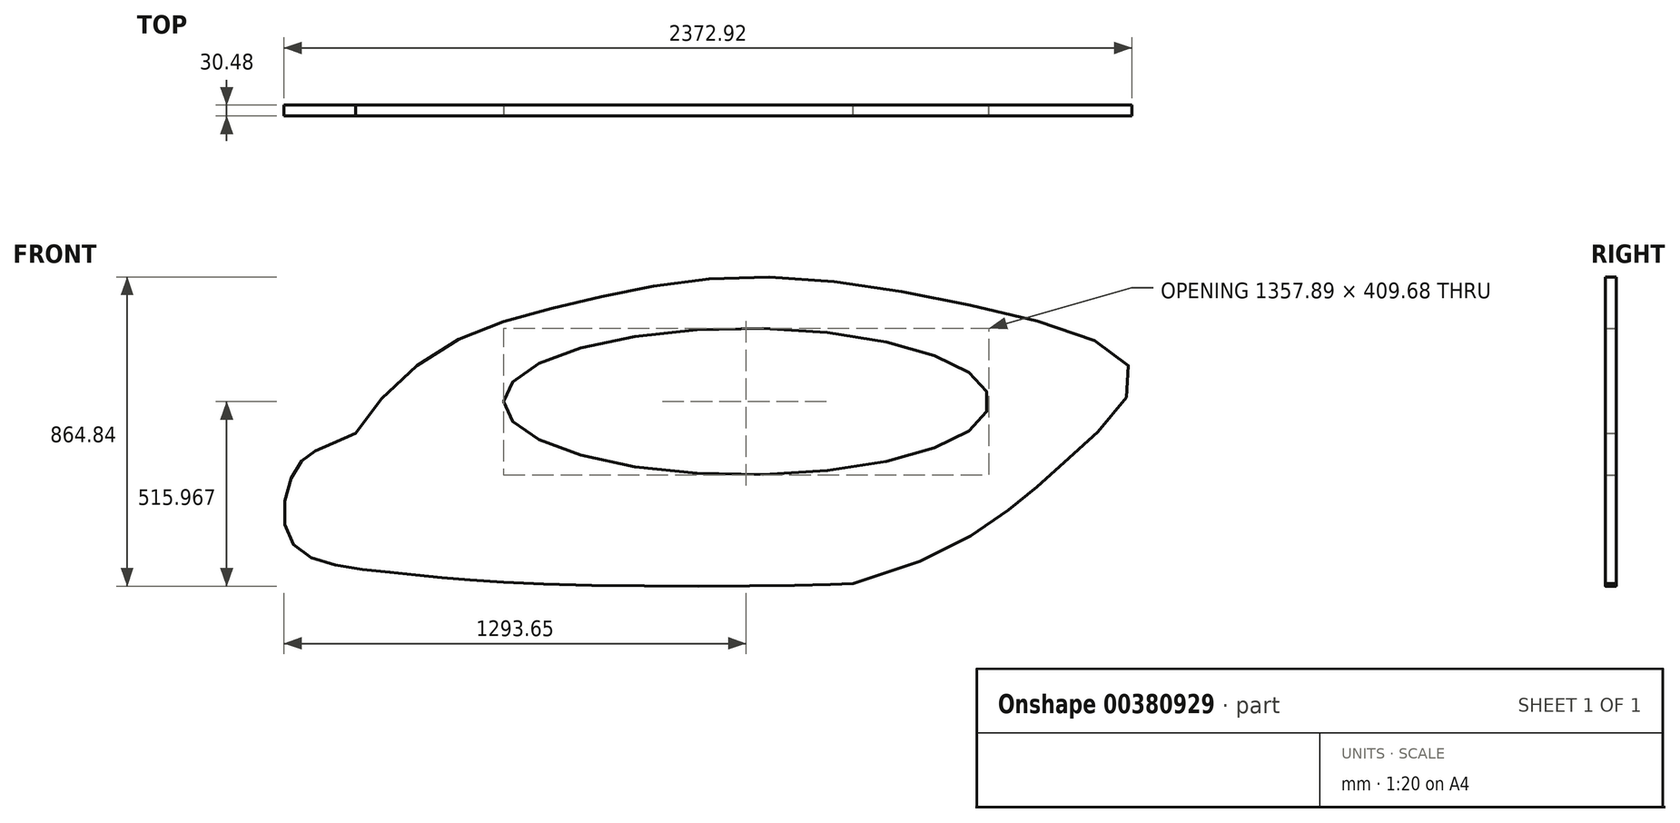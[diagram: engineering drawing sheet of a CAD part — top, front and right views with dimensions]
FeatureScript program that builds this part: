
annotation { "Feature Type Name" : "Feature", "Feature Type Description" : "" }
export const myFeature = defineFeature(function(context is Context, id is Id, definition is map)
    precondition{}
    {
        {
            var Q0;
            Q0=qCreatedBy(makeId("Front.planeOp"),FACE);
            var sketch = newSketch(context, id + "F0", { "sketchPlane" : qUnion([Q0])});
            skLineSegment(sketch, "E0.bottom", {"start": v(-2635.5, 1339.57) * mm, "end": v(-197.1, 1339.57) * mm, "construction": true});
            skLineSegment(sketch, "E0.top", {"start": v(-2635.5, 120.37) * mm, "end": v(-197.1, 120.37) * mm, "construction": true});
            skLineSegment(sketch, "E0.left", {"start": v(-2635.5, 1339.57) * mm, "end": v(-2635.5, 120.37) * mm, "construction": true});
            skLineSegment(sketch, "E0.right", {"start": v(-197.1, 1339.57) * mm, "end": v(-197.1, 120.37) * mm, "construction": true});
            skPoint(sketch, "E1.4.internal.snap0", {"position": v(-2635.5, 729.97) * mm});
            skFitSpline(sketch, "E2", {"points": [v(-2391.3, 729.97) * mm, v(-2146.72, 969.65) * mm, v(-1779.96, 1094.76) * mm, v(-1307.27, 1167.54) * mm, v(-592.3, 1070.94) * mm, v(-220.35, 894.02) * mm, v(-379.84, 674.7) * mm, v(-548.1, 529.53) * mm, v(-1000.27, 309.66) * mm], "startDerivative": vector(1299.86, 2184) * mm, "endDerivative": vector(-4926.3, -1248.1) * mm});
            skFitSpline(sketch, "E3", {"points": [v(-1000.27, 309.66) * mm, v(-1891.87, 309.66) * mm, v(-2307.3, 343.4) * mm, v(-2572.43, 428.35) * mm, v(-2551.9, 642.55) * mm, v(-2391.3, 729.97) * mm], "startDerivative": vector(-951.3, -64.03) * mm, "endDerivative": vector(1650.1, 836.12) * mm});
            skSolve(sketch);
        }
        {
            var Q0;
            Q0 = qSketchRegion(id + "F0", true);
            extrude(context, id + "F1", {"entities" : qUnion([Q0]), "depth" : 30.48 * mm});
        }
        {
            var Q0;
            Q0=makeQuery(id+"F1.opExtrude","CAP_FACE",FACE,{"disambiguationData":[OSD([sQuery(id+"F0.wireOp",EDGE,"E2"),sQuery(id+"F0.wireOp",EDGE,"E3")])],"isStart":false});
            var sketch = newSketch(context, id + "F2", { "sketchPlane" : qUnion([Q0])});
            skEllipse(sketch, "E4", {"center": v(-1298.91, 818.97) * mm, "majorRadius": 678.94 * mm, "minorRadius": 204.84 * mm, "majorAxis": v(-1, 0)});
            skSolve(sketch);
        }
        {
            var Q0;
            Q0 = qSketchRegion(id + "F2", true);
            extrude(context, id + "F3", {"entities" : qUnion([Q0]), "operationType" : NewBodyOperationType.REMOVE, "endBound" : BoundingType.THROUGH_ALL, "oppositeDirection" : true, "depth" : 30.48 * mm});
        }
    });
